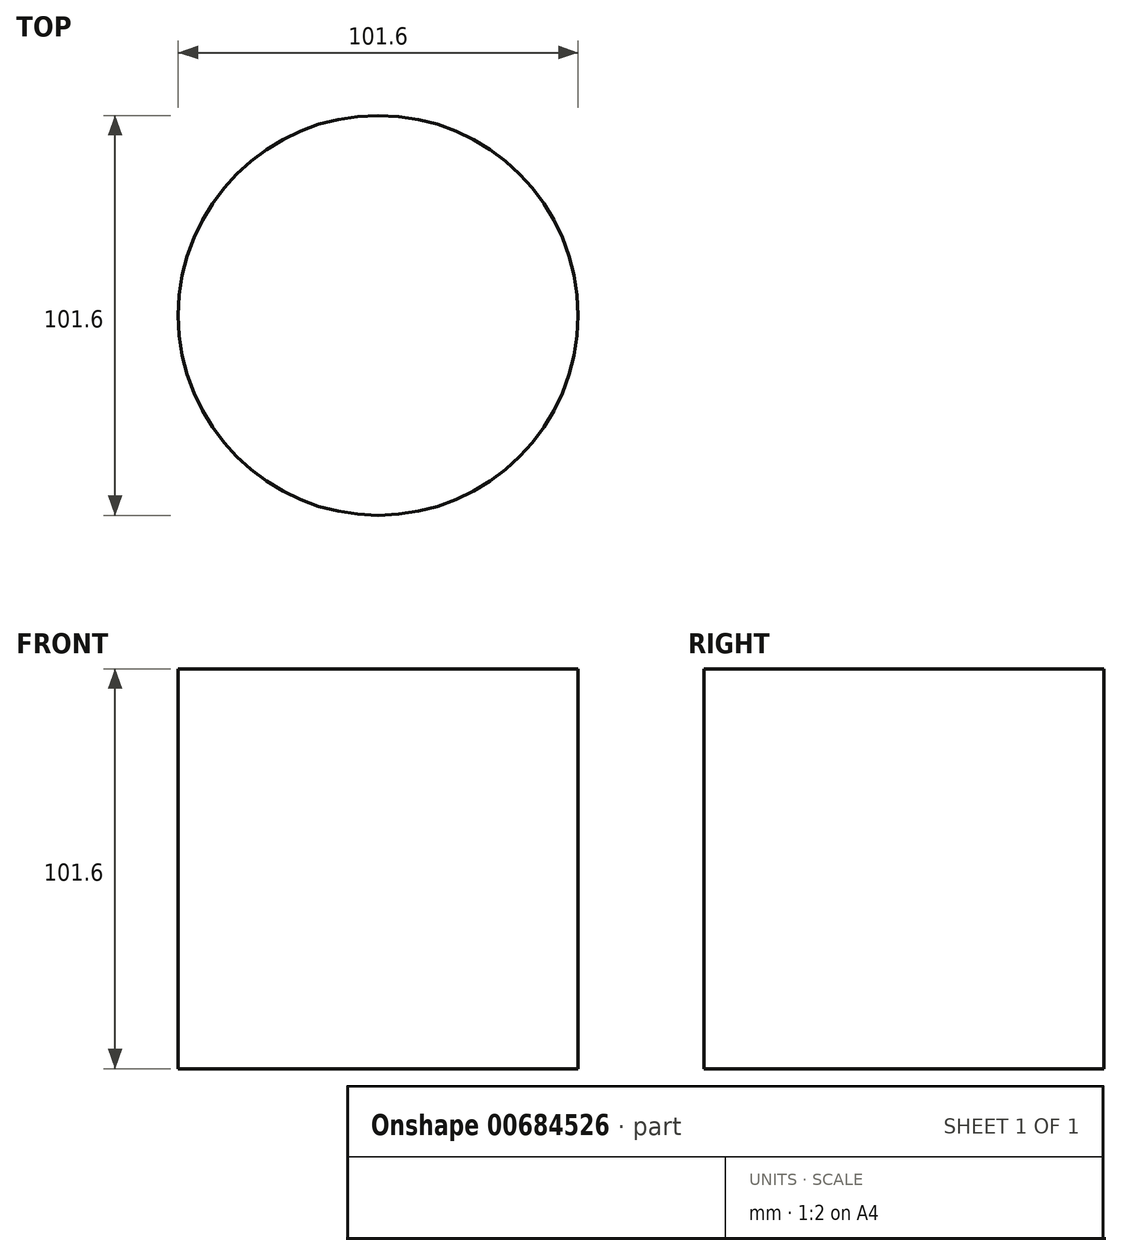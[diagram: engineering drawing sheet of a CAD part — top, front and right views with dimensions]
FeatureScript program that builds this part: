
annotation { "Feature Type Name" : "Feature", "Feature Type Description" : "" }
export const myFeature = defineFeature(function(context is Context, id is Id, definition is map)
    precondition{}
    {
        {
            var Q0;
            Q0=qCreatedBy(makeId("Top.planeOp"),FACE);
            var sketch = newSketch(context, id + "F0", { "sketchPlane" : qUnion([Q0])});
            skCircle(sketch, "E0", {"center": v(0, 0) * mm, "radius": 50.8 * mm});
            skSolve(sketch);
        }
        {
            var Q0;
            Q0 = qSketchRegion(id + "F0", true);
            extrude(context, id + "F1", {"entities" : qUnion([Q0]), "endBound" : BoundingType.SYMMETRIC, "depth" : 101.6 * mm, "offsetDistance" : 25.4 * mm});
        }
    });
